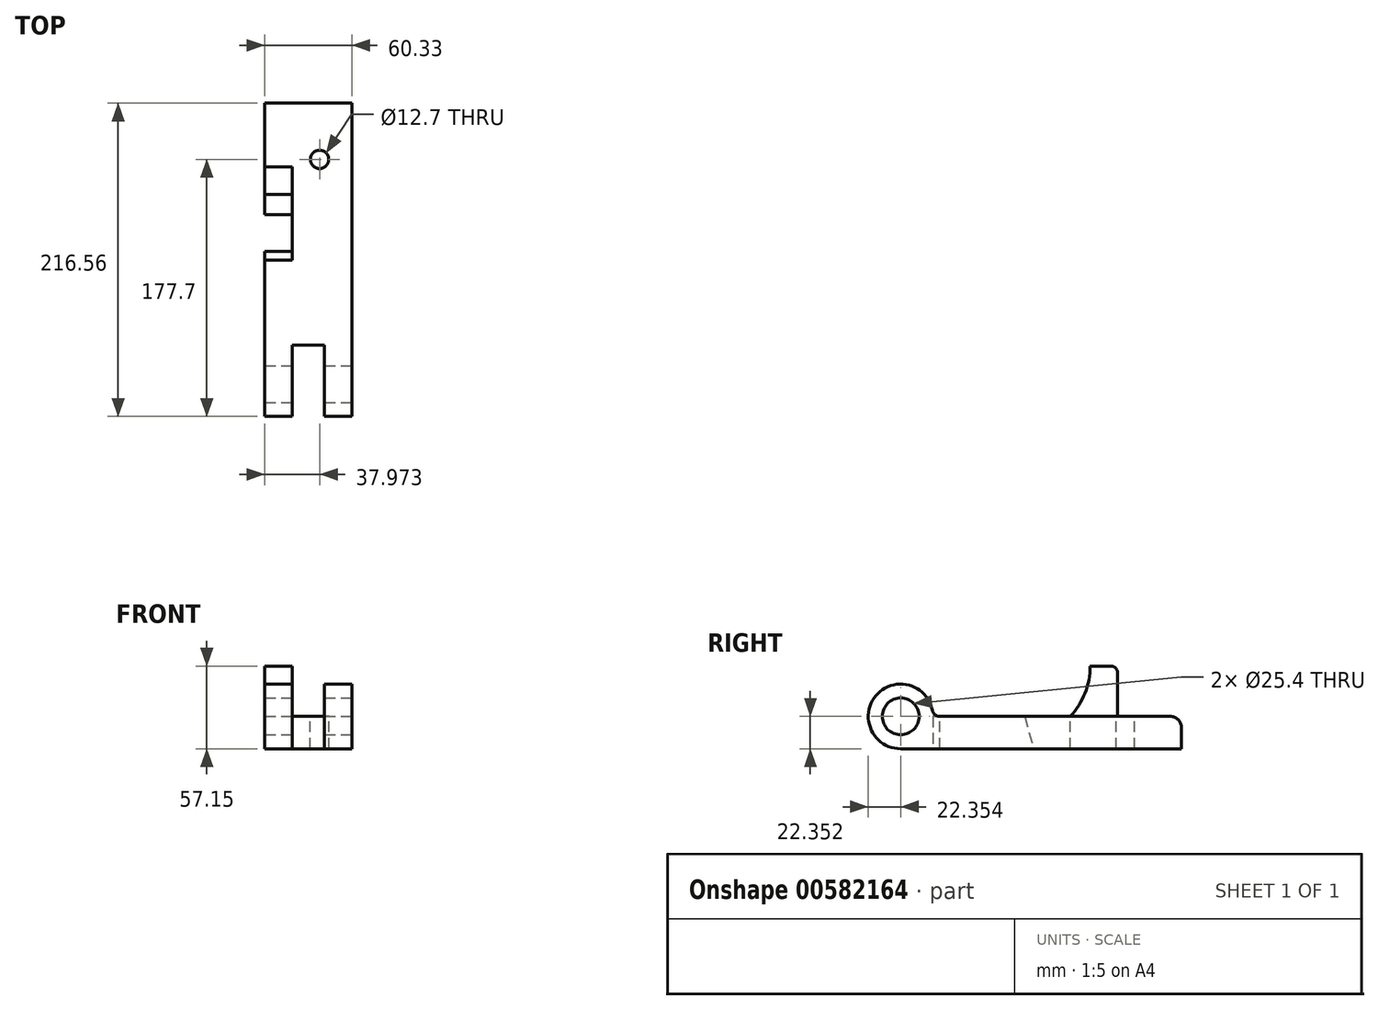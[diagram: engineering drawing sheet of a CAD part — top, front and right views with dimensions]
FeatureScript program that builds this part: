
annotation { "Feature Type Name" : "Feature", "Feature Type Description" : "" }
export const myFeature = defineFeature(function(context is Context, id is Id, definition is map)
    precondition{}
    {
        {
            var Q0;
            Q0=qCreatedBy(makeId("Right.planeOp"),FACE);
            var sketch = newSketch(context, id + "F0", { "sketchPlane" : qUnion([Q0])});
            skLineSegment(sketch, "E0", {"start": v(-117.25, 0) * mm, "end": v(-25.4, 0) * mm});
            skArc(sketch, "E1", {"start": v(-94.9, 22.35) * mm, "mid": v(-133.05, 38.16) * mm, "end": v(-117.25, 0) * mm});
            skCircle(sketch, "E2", {"center": v(-117.25, 22.35) * mm, "radius": 12.7 * mm});
            skPoint(sketch, "E3.orphan", {"position": v(76.96, 0) * mm});
            skLineSegment(sketch, "E4", {"start": v(-25.4, 0) * mm, "end": v(0, 0) * mm});
            skLineSegment(sketch, "E5", {"start": v(0, 0) * mm, "end": v(76.96, 0) * mm});
            skLineSegment(sketch, "E6", {"start": v(76.96, 0) * mm, "end": v(76.96, 22.35) * mm});
            skLineSegment(sketch, "E7", {"start": v(-117.25, 22.35) * mm, "end": v(-31.4, 22.35) * mm});
            skLineSegment(sketch, "E8", {"start": v(-31.4, 22.35) * mm, "end": v(-25.4, 0) * mm});
            skLineSegment(sketch, "E9", {"start": v(0, 0) * mm, "end": v(0, 22.35) * mm});
            skLineSegment(sketch, "E10", {"start": v(-117.25, 22.35) * mm, "end": v(-117.25, 80.8) * mm, "construction": true});
            skLineSegment(sketch, "E11", {"start": v(13.8, 57.15) * mm, "end": v(-117.25, 57.15) * mm, "construction": true});
            skArc(sketch, "E12", {"start": v(0, 22.35) * mm, "mid": v(10.22, 38.43) * mm, "end": v(13.8, 57.15) * mm});
            skLineSegment(sketch, "E13", {"start": v(-31.4, 22.35) * mm, "end": v(0, 22.35) * mm});
            skLineSegment(sketch, "E14", {"start": v(13.8, 57.15) * mm, "end": v(32.84, 57.15) * mm});
            skLineSegment(sketch, "E15", {"start": v(76.96, 22.35) * mm, "end": v(32.84, 22.35) * mm});
            skLineSegment(sketch, "E16", {"start": v(32.84, 57.15) * mm, "end": v(32.84, 22.35) * mm});
            skLineSegment(sketch, "E17", {"start": v(32.84, 22.35) * mm, "end": v(32.84, 0) * mm});
            skLineSegment(sketch, "E18", {"start": v(0, 22.35) * mm, "end": v(32.84, 22.35) * mm});
            skSolve(sketch);
        }
        {
            var Q0;
            Q0=makeQuery(id+"F0.imprint","IMPRINT",FACE,{"disambiguationData":[TD([[makeQuery(id+"F0.imprint","IMPRINT",EDGE,{"derivedFrom":sQuery(id+"F0.wireOp",EDGE,"E0")}),1.0]])]});
            extrude(context, id + "F1", {"entities" : qUnion([Q0]), "oppositeDirection" : true, "depth" : 60.32 * mm, "offsetDistance" : 25.4 * mm});
        }
        {
            var Q0;
            Q0=makeQuery(id+"F0.imprint","IMPRINT",FACE,{"disambiguationData":[TD([[makeQuery(id+"F0.imprint","IMPRINT",EDGE,{"derivedFrom":sQuery(id+"F0.wireOp",EDGE,"E4")}),1.0]])]});
            extrude(context, id + "F2", {"entities" : qUnion([Q0]), "operationType" : NewBodyOperationType.ADD, "oppositeDirection" : true, "depth" : 41.27 * mm, "offsetDistance" : 25.4 * mm});
        }
        {
            var Q0;
            Q0=makeQuery(id+"F1.opExtrude","SWEPT_BODY",BODY,{"disambiguationData":[OSD([sQuery(id+"F0.wireOp",EDGE,"E0"),sQuery(id+"F0.wireOp",EDGE,"E1"),sQuery(id+"F0.wireOp",EDGE,"E2"),sQuery(id+"F0.wireOp",EDGE,"E7"),sQuery(id+"F0.wireOp",EDGE,"E8")])]});
            transform(context, id + "F3", {"entities" : qUnion([Q0]), "transformType" : TransformType.TRANSLATION_3D, "dx" : 41.27 * mm, "dy" : 0 * mm, "dz" : 0 * mm, "makeCopy" : false});
        }
        {
            var Q0;
            {var subQ0=sQuery(id+"F0.wireOp",EDGE,"E9");Q0=makeQuery(id+"F0.imprint","IMPRINT",FACE,{"disambiguationData":[TD([[makeQuery(id+"F0.imprint","IMPRINT",EDGE,{"derivedFrom":subQ0}),-1.0]])]});}
            extrude(context, id + "F4", {"entities" : qUnion([Q0]), "operationType" : NewBodyOperationType.ADD, "depth" : 41.27 * mm, "offsetDistance" : 25.4 * mm});
        }
        {
            var Q0;
            {var subQ0=sQuery(id+"F0.wireOp",EDGE,"E9");Q0=makeQuery(id+"F0.imprint","IMPRINT",FACE,{"disambiguationData":[TD([[makeQuery(id+"F0.imprint","IMPRINT",EDGE,{"derivedFrom":subQ0}),-1.0]])]});}
            var Q1;
            Q1=makeQuery(id+"F0.imprint","IMPRINT",FACE,{"disambiguationData":[TD([[makeQuery(id+"F0.imprint","IMPRINT",EDGE,{"derivedFrom":sQuery(id+"F0.wireOp",EDGE,"E12")}),-1.0]])]});
            extrude(context, id + "F5", {"entities" : qUnion([Q0, Q1]), "operationType" : NewBodyOperationType.ADD, "oppositeDirection" : true, "depth" : 19.05 * mm, "offsetDistance" : 25.4 * mm});
        }
        {
            var Q0;
            {var subQ0=sQuery(id+"F0.wireOp",EDGE,"E6");Q0=makeQuery(id+"F0.imprint","IMPRINT",FACE,{"disambiguationData":[TD([[makeQuery(id+"F0.imprint","IMPRINT",EDGE,{"derivedFrom":subQ0}),1.0]])]});}
            extrude(context, id + "F6", {"entities" : qUnion([Q0]), "operationType" : NewBodyOperationType.ADD, "depth" : 41.27 * mm, "offsetDistance" : 25.4 * mm});
        }
        {
            var Q0;
            {var subQ0=sQuery(id+"F0.wireOp",EDGE,"E6");Q0=makeQuery(id+"F0.imprint","IMPRINT",FACE,{"disambiguationData":[TD([[makeQuery(id+"F0.imprint","IMPRINT",EDGE,{"derivedFrom":subQ0}),1.0]])]});}
            extrude(context, id + "F7", {"entities" : qUnion([Q0]), "operationType" : NewBodyOperationType.ADD, "oppositeDirection" : true, "depth" : 19.05 * mm, "offsetDistance" : 25.4 * mm});
        }
        {
            var Q0;
            Q0=qCreatedBy(makeId("Top.planeOp"),FACE);
            var sketch = newSketch(context, id + "F8", { "sketchPlane" : qUnion([Q0])});
            skLineSegment(sketch, "E19.0", {"start": v(-19.05, -94.9) * mm, "end": v(41.28, -94.9) * mm});
            skLineSegment(sketch, "E20", {"start": v(41.28, -139.6) * mm, "end": v(-19.05, -139.6) * mm});
            skLineSegment(sketch, "E21.0", {"start": v(-19.05, -94.9) * mm, "end": v(-19.05, -139.6) * mm});
            skLineSegment(sketch, "E22.0", {"start": v(41.28, -94.9) * mm, "end": v(41.28, -139.6) * mm});
            skLineSegment(sketch, "E23", {"start": v(22.28, -94.9) * mm, "end": v(22.28, -139.6) * mm});
            skLineSegment(sketch, "E24", {"start": v(-0.05, -94.9) * mm, "end": v(-0.05, -139.6) * mm});
            skLineSegment(sketch, "E25", {"start": v(-0.05, -139.6) * mm, "end": v(22.28, -139.6) * mm});
            skLineSegment(sketch, "E26", {"start": v(-0.05, -139.6) * mm, "end": v(-0.05, -94.9) * mm});
            skSolve(sketch);
        }
        {
            var Q0;
            {var subQ0=sQuery(id+"F8.wireOp",EDGE,"E23");Q0=makeQuery(id+"F8.imprint","IMPRINT",FACE,{"disambiguationData":[TD([[makeQuery(id+"F8.imprint","IMPRINT",EDGE,{"derivedFrom":subQ0}),-1.0]])]});}
            extrude(context, id + "F9", {"entities" : qUnion([Q0]), "operationType" : NewBodyOperationType.REMOVE, "depth" : 47.75 * mm, "offsetDistance" : 25.4 * mm});
        }
        {
            var Q0;
            {var subQ0=sQuery(id+"F0.wireOp",EDGE,"E15");Q0=makeQuery(id+"F7.boolean.opBoolean","MERGE",FACE,{"derivedFrom":[makeQuery(id+"F6.boolean.opBoolean","MERGE",FACE,{"derivedFrom":[makeQuery(id+"F4.boolean.opBoolean","MERGE",FACE,{"derivedFrom":[makeQuery(id+"F2.boolean.opBoolean","MERGE",FACE,{"derivedFrom":[makeQuery(id+"F1.opExtrude","SWEPT_FACE",FACE,{"disambiguationData":[OSD([sQuery(id+"F0.wireOp",EDGE,"E7")])]}),makeQuery(id+"F2.opExtrude","SWEPT_FACE",FACE,{"disambiguationData":[OSD([sQuery(id+"F0.wireOp",EDGE,"E13")])]})]}),makeQuery(id+"F4.opExtrude","SWEPT_FACE",FACE,{"disambiguationData":[OSD([sQuery(id+"F0.wireOp",EDGE,"E18")])]})]}),makeQuery(id+"F6.opExtrude","SWEPT_FACE",FACE,{"disambiguationData":[OSD([subQ0])]})]}),makeQuery(id+"F7.opExtrude","SWEPT_FACE",FACE,{"disambiguationData":[OSD([subQ0])]})]});}
            var sketch = newSketch(context, id + "F10", { "sketchPlane" : qUnion([Q0])});
            skLineSegment(sketch, "E27.0", {"start": v(41.28, 76.96) * mm, "end": v(-19.05, 76.96) * mm});
            skLineSegment(sketch, "E28.0", {"start": v(-19.05, 76.96) * mm, "end": v(-19.05, 32.84) * mm});
            skCircle(sketch, "E29", {"center": v(18.92, 38.1) * mm, "radius": 6.35 * mm});
            skLineSegment(sketch, "E30.0", {"start": v(41.28, -94.9) * mm, "end": v(41.28, 76.96) * mm});
            skSolve(sketch);
        }
        {
            var Q0;
            Q0=makeQuery(id+"F10.imprint","IMPRINT",FACE,{"disambiguationData":[TD([[makeQuery(id+"F10.imprint","IMPRINT",EDGE,{"derivedFrom":sQuery(id+"F10.wireOp",EDGE,"E29")}),1.0]])]});
            extrude(context, id + "F11", {"entities" : qUnion([Q0]), "operationType" : NewBodyOperationType.REMOVE, "oppositeDirection" : true, "depth" : 22.35 * mm, "offsetDistance" : 25.4 * mm});
        }
        {
            var Q0;
            Q0=makeQuery(id+"F5.opExtrude","SWEPT_EDGE",EDGE,{"disambiguationData":[OSD([sQuery(id+"F0.wireOp",EDGE,"E14"),sQuery(id+"F0.wireOp",EDGE,"E16")])]});
            var Q1;
            Q1=makeQuery(id+"F7.opExtrude","SWEPT_EDGE",EDGE,{"disambiguationData":[OSD([sQuery(id+"F0.wireOp",EDGE,"E15"),sQuery(id+"F0.wireOp",EDGE,"E16"),sQuery(id+"F0.wireOp",EDGE,"E17"),sQuery(id+"F0.wireOp",EDGE,"E18")])]});
            var Q2;
            {var subQ0=sQuery(id+"F0.wireOp",EDGE,"E15");var subQ1=makeQuery(id+"F7.opExtrude","SWEPT_FACE",FACE,{"disambiguationData":[OSD([subQ0])]});var subQ2=sQuery(id+"F0.wireOp",EDGE,"E18");var subQ3=makeQuery(id+"F4.opExtrude","SWEPT_FACE",FACE,{"disambiguationData":[OSD([subQ2])]});var subQ7=sQuery(id+"F0.wireOp",EDGE,"E13");var subQ8=makeQuery(id+"F2.opExtrude","SWEPT_FACE",FACE,{"disambiguationData":[OSD([subQ7])]});var subQ9=sQuery(id+"F0.wireOp",EDGE,"E7");var subQ10=makeQuery(id+"F1.opExtrude","SWEPT_FACE",FACE,{"disambiguationData":[OSD([subQ9])]});var subQ12=sQuery(id+"F0.wireOp",EDGE,"E1");var subQ13=makeQuery(id+"F6.opExtrude","SWEPT_FACE",FACE,{"disambiguationData":[OSD([subQ0])]});var subQ14=makeQuery(id+"F1.opExtrude","SWEPT_FACE",FACE,{"disambiguationData":[OSD([subQ12])]});Q2=makeQuery(id+"F9.boolean.opBoolean","SPLIT",EDGE,{"disambiguationData":[topologyDisambiguationEdgeConnected([subQ14,subQ10,subQ8,subQ3,subQ13,subQ1]),TD([makeQuery(id+"F9.opExtrude","SWEPT_FACE",FACE,{"disambiguationData":[OSD([sQuery(id+"F8.wireOp",EDGE,"E23")])]})])],"derivedFrom":makeQuery(id+"F1.opExtrude","SWEPT_EDGE",EDGE,{"disambiguationData":[OSD([subQ12,subQ9])]})});}
            var Q3;
            {var subQ0=makeQuery(id+"F2.opExtrude","SWEPT_FACE",FACE,{"disambiguationData":[OSD([sQuery(id+"F0.wireOp",EDGE,"E13")])]});var subQ1=sQuery(id+"F0.wireOp",EDGE,"E7");var subQ2=makeQuery(id+"F1.opExtrude","SWEPT_FACE",FACE,{"disambiguationData":[OSD([subQ1])]});var subQ3=sQuery(id+"F0.wireOp",EDGE,"E1");var subQ4=makeQuery(id+"F1.opExtrude","SWEPT_FACE",FACE,{"disambiguationData":[OSD([subQ3])]});var subQ5=sQuery(id+"F0.wireOp",EDGE,"E15");var subQ6=makeQuery(id+"F6.opExtrude","SWEPT_FACE",FACE,{"disambiguationData":[OSD([subQ5])]});var subQ7=makeQuery(id+"F4.opExtrude","SWEPT_FACE",FACE,{"disambiguationData":[OSD([sQuery(id+"F0.wireOp",EDGE,"E18")])]});var subQ8=makeQuery(id+"F7.opExtrude","SWEPT_FACE",FACE,{"disambiguationData":[OSD([subQ5])]});Q3=makeQuery(id+"F9.boolean.opBoolean","SPLIT",EDGE,{"disambiguationData":[topologyDisambiguationEdgeConnected([subQ4,subQ2,subQ0,subQ7,subQ6,subQ8]),TD([makeQuery(id+"F9.opExtrude","SWEPT_FACE",FACE,{"disambiguationData":[OSD([sQuery(id+"F8.wireOp",EDGE,"E26")])]})])],"derivedFrom":makeQuery(id+"F1.opExtrude","SWEPT_EDGE",EDGE,{"disambiguationData":[OSD([subQ3,subQ1])]})});}
            fillet(context, id + "F12", {"entities" : qUnion([Q0, Q1, Q2, Q3]), "radius" : 5.08 * mm, "tangentPropagation" : true, "allowEdgeOverflow" : false});
        }
        {
            var Q0;
            {var subQ0=sQuery(id+"F0.wireOp",EDGE,"E15");var subQ1=sQuery(id+"F0.wireOp",EDGE,"E6");Q0=makeQuery(id+"F7.boolean.opBoolean","MERGE",EDGE,{"derivedFrom":[makeQuery(id+"F6.opExtrude","SWEPT_EDGE",EDGE,{"disambiguationData":[OSD([subQ1,subQ0])]}),makeQuery(id+"F7.opExtrude","SWEPT_EDGE",EDGE,{"disambiguationData":[OSD([subQ1,subQ0])]})]});}
            fillet(context, id + "F13", {"entities" : qUnion([Q0]), "radius" : 7.87 * mm, "tangentPropagation" : true, "allowEdgeOverflow" : false});
        }
        {
            var Q0;
            {var subQ0=sQuery(id+"F0.wireOp",EDGE,"E15");Q0=makeQuery(id+"F7.boolean.opBoolean","MERGE",FACE,{"derivedFrom":[makeQuery(id+"F6.boolean.opBoolean","MERGE",FACE,{"derivedFrom":[makeQuery(id+"F4.boolean.opBoolean","MERGE",FACE,{"derivedFrom":[makeQuery(id+"F2.boolean.opBoolean","MERGE",FACE,{"derivedFrom":[makeQuery(id+"F1.opExtrude","SWEPT_FACE",FACE,{"disambiguationData":[OSD([sQuery(id+"F0.wireOp",EDGE,"E7")])]}),makeQuery(id+"F2.opExtrude","SWEPT_FACE",FACE,{"disambiguationData":[OSD([sQuery(id+"F0.wireOp",EDGE,"E13")])]})]}),makeQuery(id+"F4.opExtrude","SWEPT_FACE",FACE,{"disambiguationData":[OSD([sQuery(id+"F0.wireOp",EDGE,"E18")])]})]}),makeQuery(id+"F6.opExtrude","SWEPT_FACE",FACE,{"disambiguationData":[OSD([subQ0])]})]}),makeQuery(id+"F7.opExtrude","SWEPT_FACE",FACE,{"disambiguationData":[OSD([subQ0])]})]});}
            var sketch = newSketch(context, id + "F14", { "sketchPlane" : qUnion([Q0])});
            skLineSegment(sketch, "E31.0", {"start": v(22.28, -94.9) * mm, "end": v(-0.05, -94.9) * mm});
            skLineSegment(sketch, "E32.0", {"start": v(0, -117.25) * mm, "end": v(0, -31.4) * mm});
            skLineSegment(sketch, "E33.0", {"start": v(22.28, -95.28) * mm, "end": v(22.28, -90.29) * mm});
            skLineSegment(sketch, "E34", {"start": v(22.28, -90.29) * mm, "end": v(-0.05, -90.29) * mm});
            skSolve(sketch);
        }
        {
            var Q0;
            {var subQ0=sQuery(id+"F14.wireOp",EDGE,"E33.0");var subQ1=sQuery(id+"F14.wireOp",EDGE,"E31.0");var subQ2=makeQuery(id+"F14.imprint","INTERSECT",VERTEX,{"derivedFrom":[subQ1,subQ0]});Q0=makeQuery(id+"F14.imprint","IMPRINT",FACE,{"disambiguationData":[TD([[makeQuery(id+"F14.imprint","IMPRINT",EDGE,{"disambiguationData":[TD([[subQ2,-1.0]])],"derivedFrom":subQ1}),-1.0]])]});}
            extrude(context, id + "F15", {"entities" : qUnion([Q0]), "operationType" : NewBodyOperationType.REMOVE, "oppositeDirection" : true, "depth" : 22.35 * mm, "offsetDistance" : 25.4 * mm});
        }
    });
